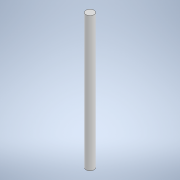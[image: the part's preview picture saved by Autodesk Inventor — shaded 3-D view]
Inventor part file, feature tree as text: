
AUTODESK INVENTOR PART (.ipt)
format: ipt  version: 2021 (Build 250183000, 183)  size: 91,136 bytes
history: native  units: mm
features: extrude x1, sketch x1
ambient origin geometry x8: Origin, YZ Plane, XZ Plane, XY Plane, X Axis, Y Axis, Z Axis, Center Point
bodies: Solid1 (feature_tree)
feature tree (2):
  extrude  "Extrusion1"  Depth=50.0mm TaperAngle=0.0deg
  sketch  "Sketch1"  dims[d0=3.0mm d1=50.0mm d2=0.0mm]
